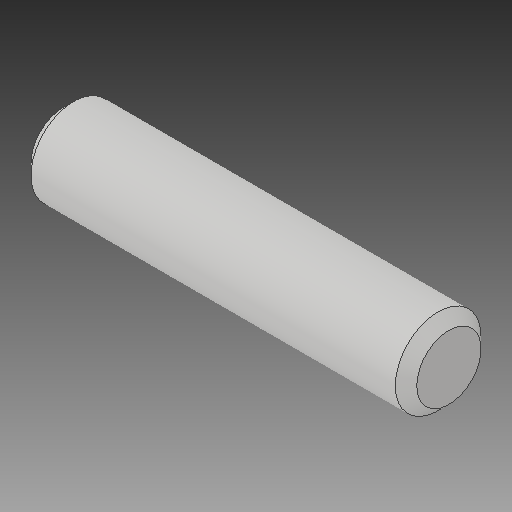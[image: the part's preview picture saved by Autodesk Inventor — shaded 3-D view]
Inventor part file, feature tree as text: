
AUTODESK INVENTOR PART (.ipt)
format: ipt  version: 2017 (Build 210142000, 142)  size: 87,040 bytes
history: native  units: in
note: dims shown in document units (in); Inventor stores cm internally (conversion verified against a paired STEP export)
features: chamfer x1
ambient origin geometry x8: Origin, YZ Plane, XZ Plane, XY Plane, X Axis, Y Axis, Z Axis, Center Point
bodies: Solid1 (feature_tree)
feature tree (1):
  chamfer  "Chamfer1"  [1 undecoded]
note: 1 required parameter value undecoded (feature->parameter linkage not recoverable at this tier; creation-order binding heuristic only, values carry confidence <= 0.55)
